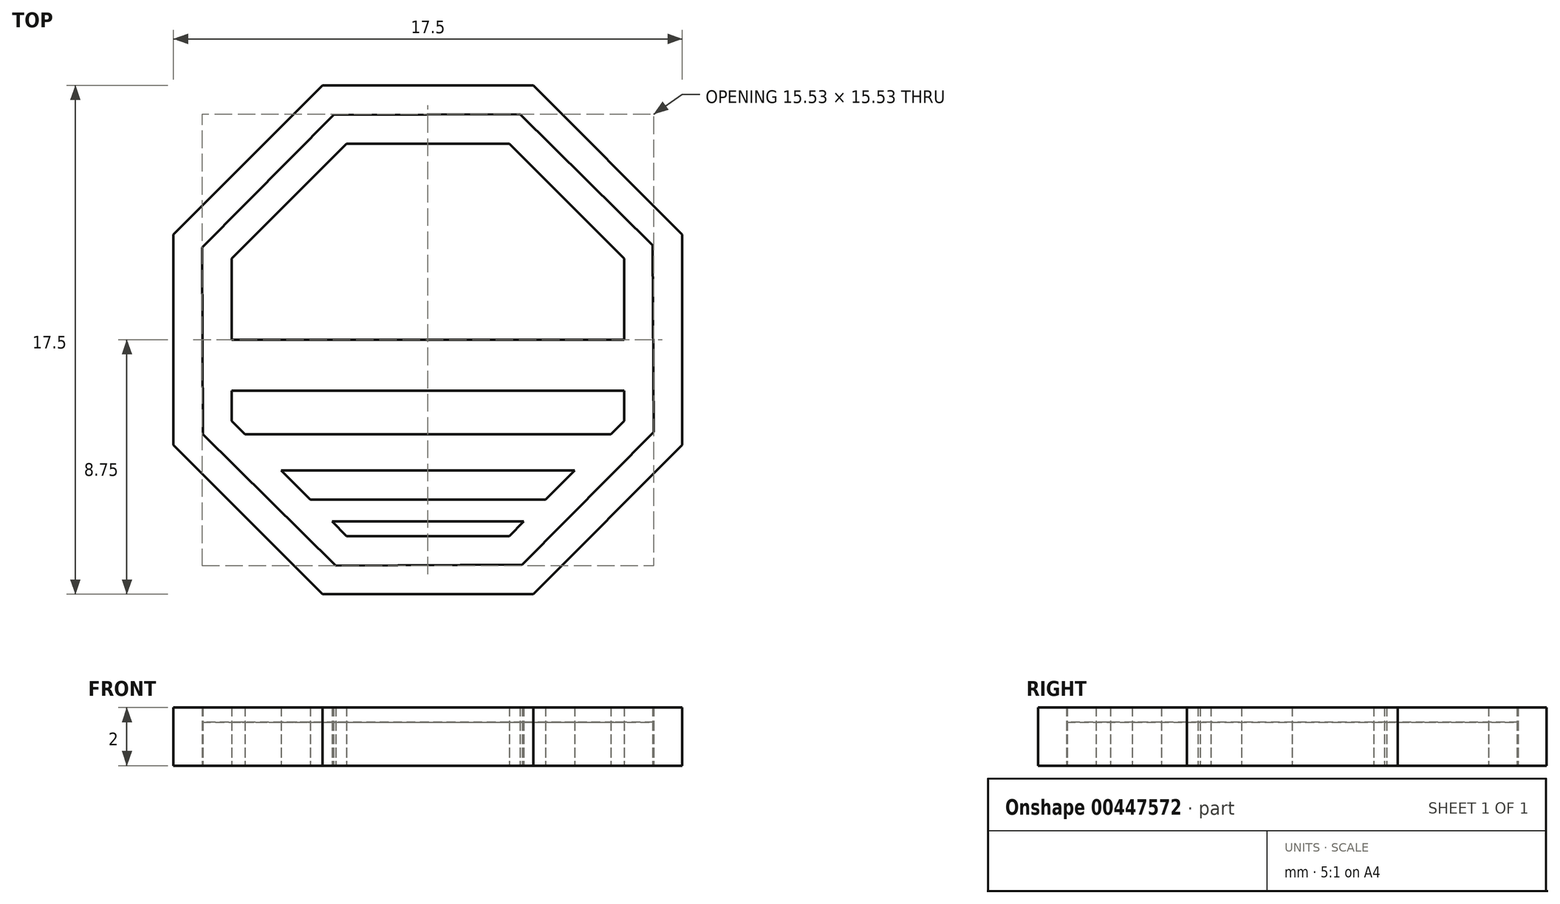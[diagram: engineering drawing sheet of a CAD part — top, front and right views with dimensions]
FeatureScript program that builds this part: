
annotation { "Feature Type Name" : "Feature", "Feature Type Description" : "" }
export const myFeature = defineFeature(function(context is Context, id is Id, definition is map)
    precondition{}
    {
        {
            var Q0;
            Q0=qCreatedBy(makeId("Top.planeOp"),FACE);
            var sketch = newSketch(context, id + "F0", { "sketchPlane" : qUnion([Q0])});
            skCircle(sketch, "E0.cCircle", {"center": v(0, 0) * mm, "radius": 8.75 * mm, "construction": true});
            skLineSegment(sketch, "E0.0", {"start": v(8.75, -3.62) * mm, "end": v(3.62, -8.75) * mm});
            skLineSegment(sketch, "E0.1", {"start": v(3.62, -8.75) * mm, "end": v(-3.62, -8.75) * mm});
            skLineSegment(sketch, "E0.2", {"start": v(-3.62, -8.75) * mm, "end": v(-8.75, -3.62) * mm});
            skLineSegment(sketch, "E0.3", {"start": v(-8.75, -3.62) * mm, "end": v(-8.75, 3.62) * mm});
            skLineSegment(sketch, "E0.4", {"start": v(-8.75, 3.62) * mm, "end": v(-3.62, 8.75) * mm});
            skLineSegment(sketch, "E0.5", {"start": v(-3.62, 8.75) * mm, "end": v(3.62, 8.75) * mm});
            skLineSegment(sketch, "E0.6", {"start": v(3.62, 8.75) * mm, "end": v(8.75, 3.62) * mm});
            skLineSegment(sketch, "E0.7", {"start": v(8.75, 3.62) * mm, "end": v(8.75, -3.62) * mm});
            skPoint(sketch, "E0.0.midPoint", {"position": v(6.19, -6.19) * mm});
            skCircle(sketch, "E1.cCircle", {"center": v(0, 0) * mm, "radius": 7.75 * mm, "construction": true});
            skLineSegment(sketch, "E1.0", {"start": v(7.77, -3.17) * mm, "end": v(3.25, -7.73) * mm});
            skLineSegment(sketch, "E1.1", {"start": v(3.25, -7.73) * mm, "end": v(-3.17, -7.77) * mm});
            skLineSegment(sketch, "E1.2", {"start": v(-3.17, -7.77) * mm, "end": v(-7.73, -3.25) * mm});
            skLineSegment(sketch, "E1.3", {"start": v(-7.73, -3.25) * mm, "end": v(-7.77, 3.17) * mm});
            skLineSegment(sketch, "E1.4", {"start": v(-7.77, 3.17) * mm, "end": v(-3.25, 7.73) * mm});
            skLineSegment(sketch, "E1.5", {"start": v(-3.25, 7.73) * mm, "end": v(3.17, 7.77) * mm});
            skLineSegment(sketch, "E1.6", {"start": v(3.17, 7.77) * mm, "end": v(7.73, 3.25) * mm});
            skLineSegment(sketch, "E1.7", {"start": v(7.73, 3.25) * mm, "end": v(7.77, -3.17) * mm});
            skPoint(sketch, "E1.0.midPoint", {"position": v(5.5, -5.45) * mm});
            skCircle(sketch, "E2.cCircle", {"center": v(0, 0) * mm, "radius": 6.75 * mm, "construction": true});
            skLineSegment(sketch, "E2.0", {"start": v(6.75, -2.8) * mm, "end": v(6.3, -3.25) * mm});
            skLineSegment(sketch, "E2.1", {"start": v(2.8, -6.75) * mm, "end": v(-2.8, -6.75) * mm});
            skLineSegment(sketch, "E2.2", {"start": v(-2.8, -6.75) * mm, "end": v(-3.3, -6.25) * mm});
            skLineSegment(sketch, "E2.3", {"start": v(-6.75, -2.8) * mm, "end": v(-6.75, -1.75) * mm});
            skLineSegment(sketch, "E2.4", {"start": v(-6.75, 2.8) * mm, "end": v(-2.8, 6.75) * mm});
            skLineSegment(sketch, "E2.5", {"start": v(-2.8, 6.75) * mm, "end": v(2.8, 6.75) * mm});
            skLineSegment(sketch, "E2.6", {"start": v(2.8, 6.75) * mm, "end": v(6.75, 2.8) * mm});
            skLineSegment(sketch, "E2.7", {"start": v(6.75, 2.8) * mm, "end": v(6.75, 0) * mm});
            skPoint(sketch, "E2.0.midPoint", {"position": v(4.77, -4.77) * mm});
            skLineSegment(sketch, "E3", {"start": v(-6.75, -1.75) * mm, "end": v(6.75, -1.75) * mm});
            skLineSegment(sketch, "E4", {"start": v(-6.3, -3.25) * mm, "end": v(6.3, -3.25) * mm});
            skLineSegment(sketch, "E5", {"start": v(-6.75, 0) * mm, "end": v(6.75, 0) * mm});
            skLineSegment(sketch, "E6", {"start": v(-5.05, -4.5) * mm, "end": v(5.05, -4.5) * mm});
            skLineSegment(sketch, "E7", {"start": v(-4.05, -5.5) * mm, "end": v(4.05, -5.5) * mm});
            skLineSegment(sketch, "E8", {"start": v(-3.3, -6.25) * mm, "end": v(3.3, -6.25) * mm});
            skLineSegment(sketch, "E9.trimOffspring", {"start": v(-6.75, 0) * mm, "end": v(-6.75, 2.8) * mm});
            skLineSegment(sketch, "E10.trimOffspring", {"start": v(6.75, -1.75) * mm, "end": v(6.75, -2.8) * mm});
            skLineSegment(sketch, "E11.trimOffspring", {"start": v(5.05, -4.5) * mm, "end": v(4.05, -5.5) * mm});
            skLineSegment(sketch, "E12.trimOffspring", {"start": v(-6.3, -3.25) * mm, "end": v(-6.75, -2.8) * mm});
            skLineSegment(sketch, "E13.trimOffspring", {"start": v(-4.05, -5.5) * mm, "end": v(-5.05, -4.5) * mm});
            skLineSegment(sketch, "E14.trimOffspring", {"start": v(3.3, -6.25) * mm, "end": v(2.8, -6.75) * mm});
            skSolve(sketch);
        }
        {
            var Q0;
            Q0=makeQuery(id+"F0.imprint","IMPRINT",FACE,{"disambiguationData":[TD([[makeQuery(id+"F0.imprint","IMPRINT",EDGE,{"derivedFrom":sQuery(id+"F0.wireOp",EDGE,"E0.0")}),-1.0]])]});
            var Q1;
            Q1=makeQuery(id+"F0.imprint","IMPRINT",FACE,{"disambiguationData":[TD([[makeQuery(id+"F0.imprint","IMPRINT",EDGE,{"derivedFrom":sQuery(id+"F0.wireOp",EDGE,"E2.4")}),-1.0]])]});
            var Q2;
            Q2=makeQuery(id+"F0.imprint","IMPRINT",FACE,{"disambiguationData":[TD([[makeQuery(id+"F0.imprint","IMPRINT",EDGE,{"derivedFrom":sQuery(id+"F0.wireOp",EDGE,"E2.0")}),-1.0]])]});
            var Q3;
            Q3=makeQuery(id+"F0.imprint","IMPRINT",FACE,{"disambiguationData":[TD([[makeQuery(id+"F0.imprint","IMPRINT",EDGE,{"derivedFrom":sQuery(id+"F0.wireOp",EDGE,"E6")}),-1.0]])]});
            var Q4;
            Q4=makeQuery(id+"F0.imprint","IMPRINT",FACE,{"disambiguationData":[TD([[makeQuery(id+"F0.imprint","IMPRINT",EDGE,{"derivedFrom":sQuery(id+"F0.wireOp",EDGE,"E2.1")}),-1.0]])]});
            extrude(context, id + "F1", {"entities" : qUnion([Q0, Q1, Q2, Q3, Q4]), "depth" : 2 * mm});
        }
        {
            var Q0;
            Q0=makeQuery(id+"F0.imprint","IMPRINT",FACE,{"disambiguationData":[TD([[makeQuery(id+"F0.imprint","IMPRINT",EDGE,{"derivedFrom":sQuery(id+"F0.wireOp",EDGE,"E1.0")}),-1.0]])]});
            extrude(context, id + "F2", {"entities" : qUnion([Q0]), "depth" : 1.5 * mm});
        }
    });
